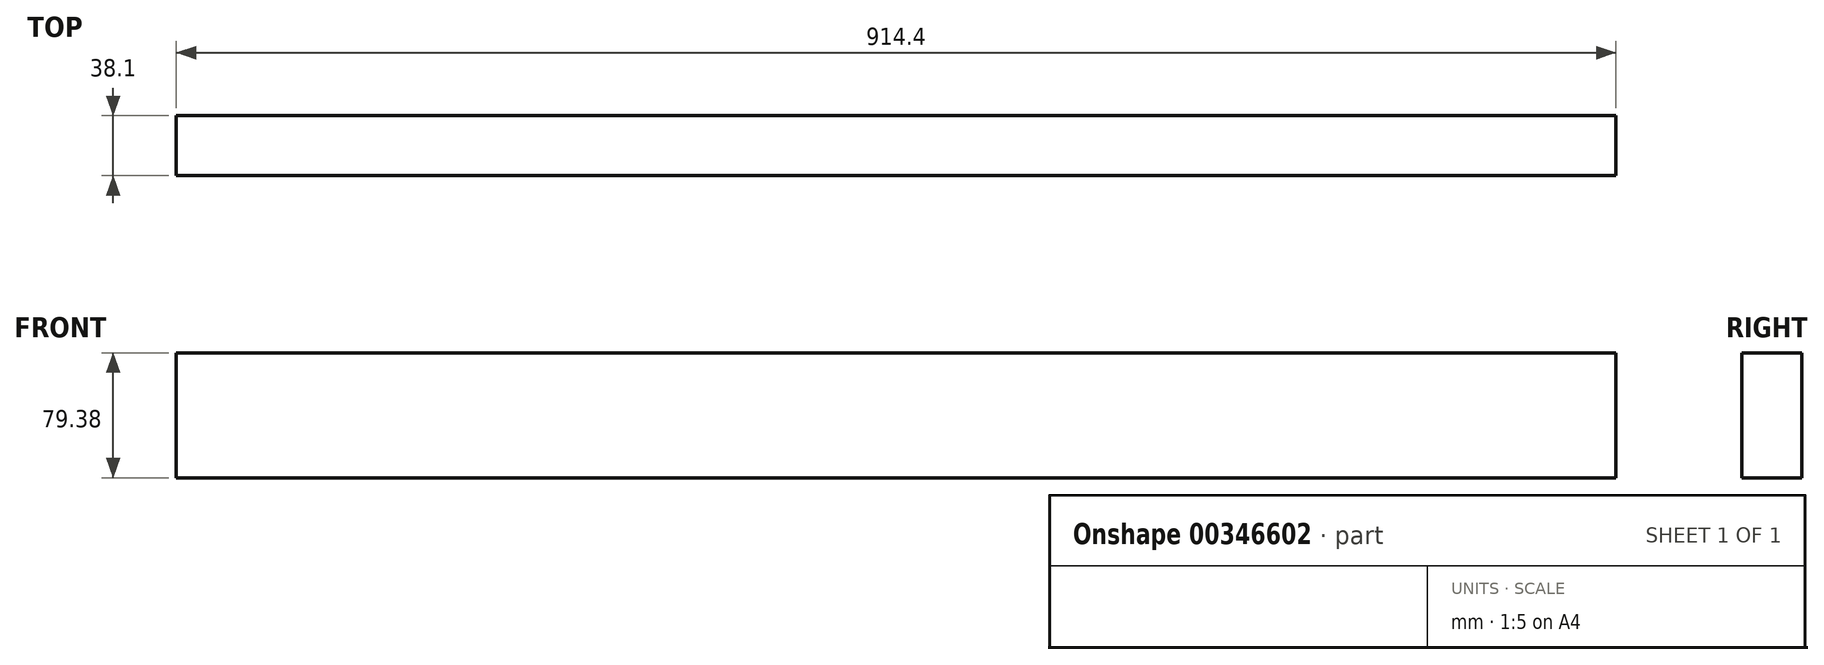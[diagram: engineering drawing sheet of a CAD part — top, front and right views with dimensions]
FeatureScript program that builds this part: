
annotation { "Feature Type Name" : "Feature", "Feature Type Description" : "" }
export const myFeature = defineFeature(function(context is Context, id is Id, definition is map)
    precondition{}
    {
        {
            var Q0;
            Q0=qCreatedBy(makeId("Right.planeOp"),FACE);
            var sketch = newSketch(context, id + "F0", { "sketchPlane" : qUnion([Q0])});
            skLineSegment(sketch, "E0.bottom", {"start": v(19.05, -39.69) * mm, "end": v(-19.05, -39.69) * mm});
            skLineSegment(sketch, "E0.top", {"start": v(19.05, 39.69) * mm, "end": v(-19.05, 39.69) * mm});
            skLineSegment(sketch, "E0.left", {"start": v(19.05, -39.69) * mm, "end": v(19.05, 39.69) * mm});
            skLineSegment(sketch, "E0.right", {"start": v(-19.05, -39.69) * mm, "end": v(-19.05, 39.69) * mm});
            skPoint(sketch, "E0.middle", {"position": v(0, 0) * mm});
            skSolve(sketch);
        }
        {
            var Q0;
            Q0=makeQuery(id+"F0.imprint","IMPRINT",FACE,{"disambiguationData":[TD([[makeQuery(id+"F0.imprint","IMPRINT",EDGE,{"derivedFrom":sQuery(id+"F0.wireOp",EDGE,"E0.bottom")}),-1.0]])]});
            extrude(context, id + "F1", {"entities" : qUnion([Q0]), "depth" : 914.4 * mm});
        }
    });
